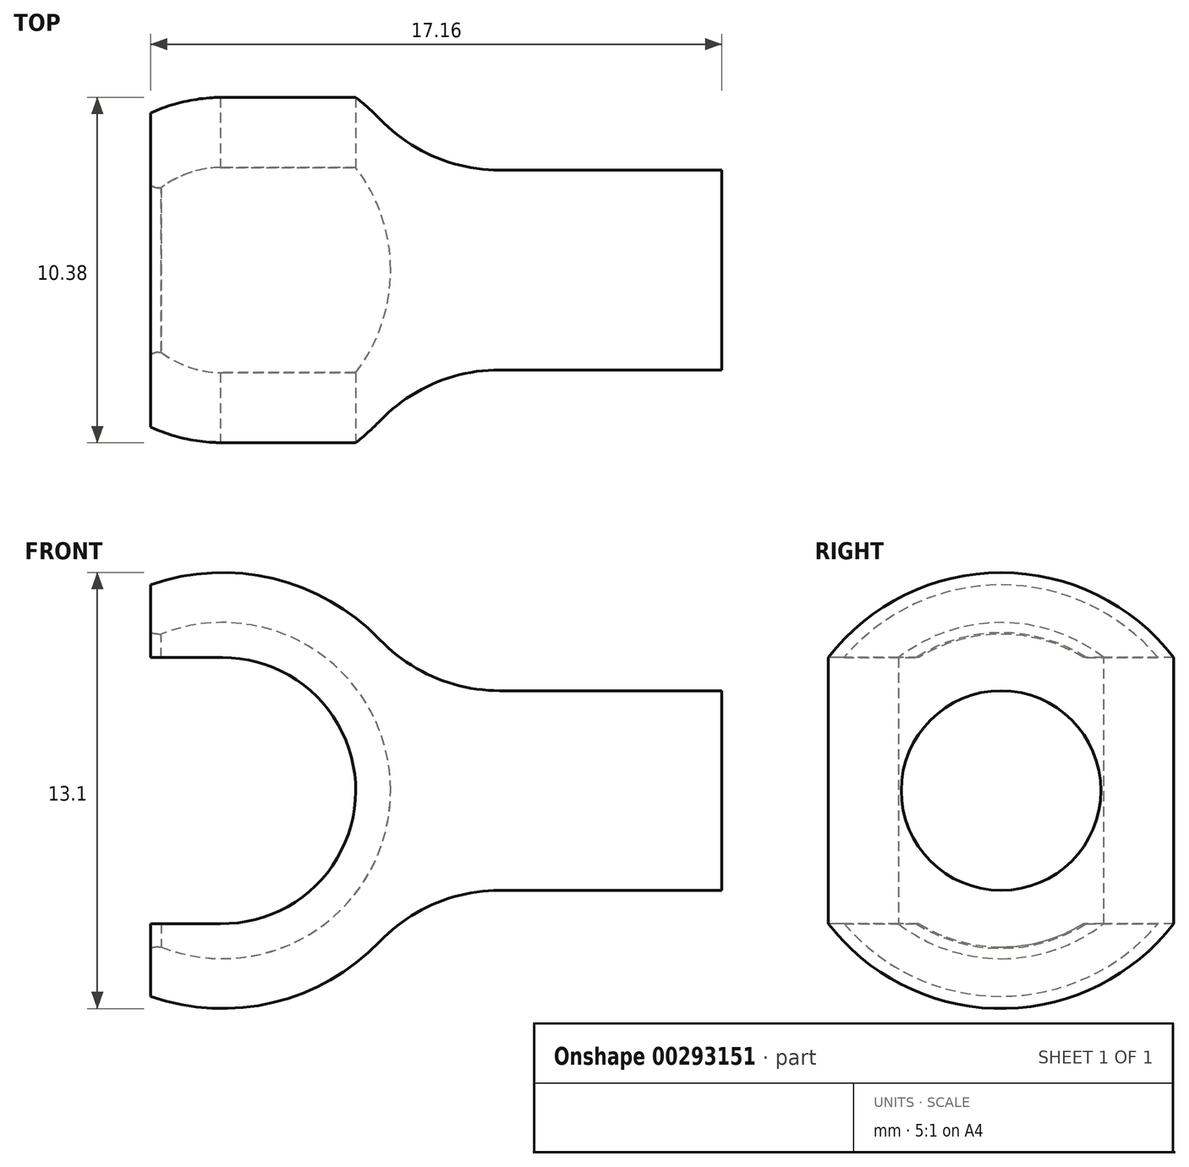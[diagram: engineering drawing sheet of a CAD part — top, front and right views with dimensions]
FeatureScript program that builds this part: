
annotation { "Feature Type Name" : "Feature", "Feature Type Description" : "" }
export const myFeature = defineFeature(function(context is Context, id is Id, definition is map)
    precondition{}
    {
        {
            var Q0;
            Q0=qCreatedBy(makeId("Front.planeOp"),FACE);
            var sketch = newSketch(context, id + "F0", { "sketchPlane" : qUnion([Q0])});
            skLineSegment(sketch, "E0", {"start": v(0, 0) * mm, "end": v(-9.95, 0) * mm});
            skLineSegment(sketch, "E1", {"start": v(0, 0) * mm, "end": v(0, -3) * mm});
            skLineSegment(sketch, "E2.0", {"start": v(0, -3) * mm, "end": v(-9.18, -3) * mm});
            skArc(sketch, "E3.trimOffspring", {"start": v(-17.16, -6.18) * mm, "mid": v(-12.58, -6.08) * mm, "end": v(-9.18, -3) * mm});
            skArc(sketch, "E4.trimOffspring", {"start": v(-16.85, -4.7) * mm, "mid": v(-12.16, -4.17) * mm, "end": v(-9.95, 0) * mm});
            skLineSegment(sketch, "E5.trimOffspring", {"start": v(-16.85, -4.7) * mm, "end": v(-16.91, -4.7) * mm});
            skPoint(sketch, "E6.visualSharp", {"position": v(-19.56, -4.7) * mm});
            skArc(sketch, "E6.filletArc", {"start": v(-16.91, -4.7) * mm, "mid": v(-17.04, -4.71) * mm, "end": v(-17.16, -4.74) * mm});
            skLineSegment(sketch, "E7", {"start": v(-17.16, -6.18) * mm, "end": v(-17.16, -4.74) * mm});
            skSolve(sketch);
        }
        {
            var Q0;
            Q0=qSketchRegion(id+"F0",true);
            var Q1;
            Q1=sQuery(id+"F0.wireOp",EDGE,"E0");
            revolve(context, id + "F1", {"entities" : qUnion([Q0]), "axis" : qUnion([Q1]), "revolveType" : RevolveType.FULL});
        }
        {
            var Q0;
            Q0=qCreatedBy(makeId("Front.planeOp"),FACE);
            var sketch = newSketch(context, id + "F2", { "sketchPlane" : qUnion([Q0])});
            skPoint(sketch, "E8.center.orphan", {"position": v(-13.79, 0) * mm});
            skArc(sketch, "E9", {"start": v(-15.06, -4) * mm, "mid": v(-11, -0.03) * mm, "end": v(-15, 4) * mm});
            skLineSegment(sketch, "E10", {"start": v(-15.06, -4) * mm, "end": v(-18.56, -4) * mm});
            skLineSegment(sketch, "E11", {"start": v(-15, 4) * mm, "end": v(-18.58, 4) * mm});
            skPoint(sketch, "E12.orphan", {"position": v(-15, 5.07) * mm});
            skLineSegment(sketch, "E13", {"start": v(-18.58, 4) * mm, "end": v(-18.56, -4) * mm});
            skPoint(sketch, "E13.endSnap0", {"position": v(-19.2, -4) * mm});
            skPoint(sketch, "E14.orphan", {"position": v(-22.15, 3.99) * mm});
            skPoint(sketch, "E15.orphan", {"position": v(-23.34, -4) * mm});
            skSolve(sketch);
        }
        {
            var Q0;
            Q0=qSketchRegion(id+"F2",true);
            extrude(context, id + "F3", {"entities" : qUnion([Q0]), "operationType" : NewBodyOperationType.REMOVE, "endBound" : BoundingType.SYMMETRIC, "oppositeDirection" : true, "depth" : 25 * mm});
        }
        {
            var Q0;
            Q0=makeQuery(id+"F1.opRevolve","SWEPT_EDGE",EDGE,{"disambiguationData":[OSD([sQuery(id+"F0.wireOp",EDGE,"E2.0"),sQuery(id+"F0.wireOp",EDGE,"E3.trimOffspring")])]});
            fillet(context, id + "F4", {"entities" : qUnion([Q0]), "radius" : 5 * mm, "tangentPropagation" : true, "allowEdgeOverflow" : false});
        }
    });
